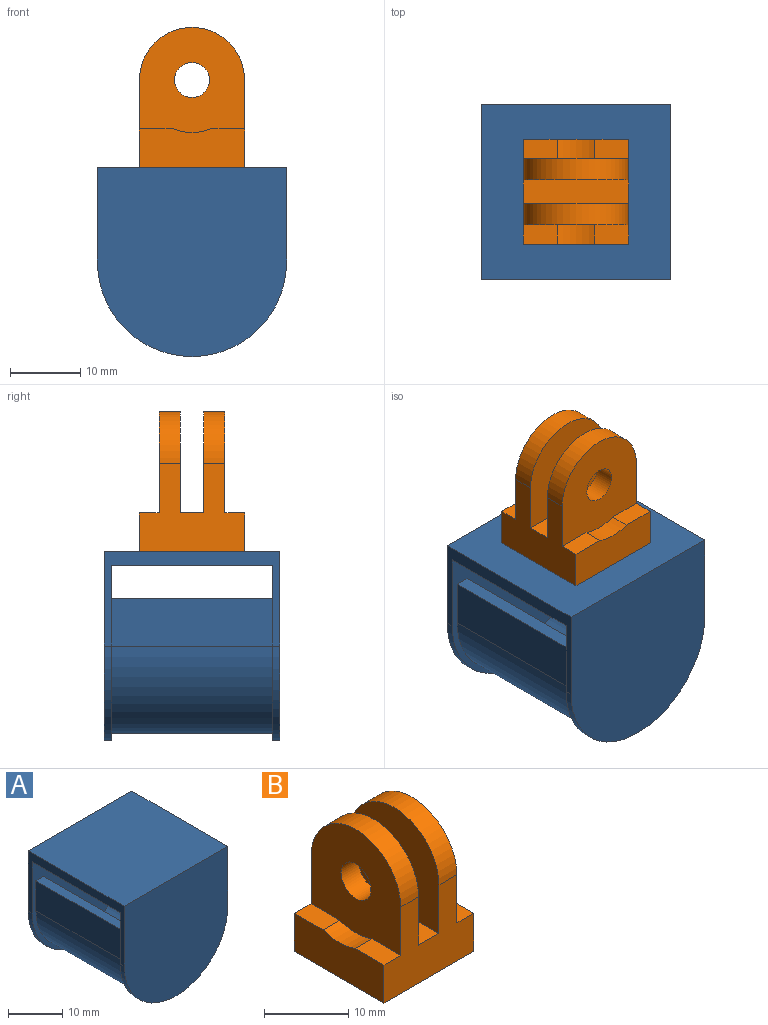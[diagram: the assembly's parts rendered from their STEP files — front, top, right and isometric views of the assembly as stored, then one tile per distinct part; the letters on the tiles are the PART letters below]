
ASSEMBLY  parts=2 mates=1
PART A: 18 faces, bbox 27x25x27 mm
  f0: plane 23x6.75mm, normal (1,0,0), area 155.2mm2, adj f3,f11,f13,f17
  f1: plane 27x23mm, normal (0,0,-1), area 621mm2, adj f4,f6,f13,f17
  f2: plane 23x6.75mm, normal (-1,0,0), area 155.2mm2, adj f3,f12,f13,f17
  f3: cylinder r=12.5mm len=25mm, axis (0,1,0), area 903.2mm2, adj f0,f2,f13,f17
  f4: plane 25x13.5mm, normal (1,0,0), area 73mm2, adj f1,f5,f7,f8,f9,f10,f13,f17
  f5: plane 27x25mm, normal (0,0,1), area 675mm2, adj f4,f6,f7,f8
  f6: plane 25x13.5mm, normal (-1,0,0), area 73mm2, adj f1,f5,f7,f8,f9,f10,f13,f17
  f7: plane 27x27mm, normal (0,-1,0), area 650.8mm2, adj f4,f5,f6,f10
  f8: plane 27x27mm, normal (0,1,0), area 650.8mm2, adj f4,f5,f6,f9
  f9: cylinder r=13.5mm len=27mm, axis (0,1,0), area 42.4mm2, adj f4,f6,f8,f13
  f10: cylinder r=13.5mm len=27mm, axis (0,1,0), area 42.4mm2, adj f4,f6,f7,f17
  f11: plane 23x2mm, normal (0,0,1), area 46mm2, adj f0,f13,f15,f17
  f12: plane 23x2mm, normal (0,0,1), area 46mm2, adj f2,f13,f14,f17
  f13: plane 27x25mm, normal (0,-1,0), area 497.5mm2, adj f0,f1,f2,f3,f4,f6,f9,f11
  f14: plane 23x6.75mm, normal (1,0,0), area 155.2mm2, adj f12,f13,f16,f17
  f15: plane 23x6.75mm, normal (-1,0,0), area 155.2mm2, adj f11,f13,f16,f17
  f16: cylinder r=10.5mm len=23mm, axis (0,1,0), area 758.7mm2, adj f13,f14,f15,f17
  f17: plane 27x25mm, normal (0,1,0), area 497.5mm2, adj f0,f1,f2,f3,f4,f6,f10,f11
PART B: 20 faces, bbox 15x15x20 mm
  f0: plane 4.81x2.8mm, normal (0,0,1), area 13.5mm2, adj f3,f8,f11,f19
  f1: plane 15x5.5mm, normal (-1,0,0), area 80.7mm2, adj f2,f3,f6,f7,f9,f18
  f2: plane 4.81x2.8mm, normal (0,0,1), area 13.5mm2, adj f1,f6,f10,f18
  f3: plane 15x12.5mm, normal (0,1,0), area 124.5mm2, adj f0,f1,f4,f5,f7,f8,f9,f10
  f4: cylinder r=7.5mm len=15mm, axis (-1,0,0), area 70.7mm2, adj f3,f6,f11,f14
  f5: cylinder r=7.5mm len=15mm, axis (-1,0,0), area 70.7mm2, adj f3,f6,f10,f15
  f6: plane 15x12.5mm, normal (0,-1,0), area 124.5mm2, adj f1,f2,f4,f5,f7,f8,f10,f11
  f7: plane 15x15mm, normal (0,0,-1), area 225mm2, adj f1,f3,f6,f8
  f8: plane 15x5.5mm, normal (1,0,0), area 80.7mm2, adj f0,f3,f6,f7,f12,f19
  f9: plane 4.81x2.8mm, normal (0,0,1), area 13.5mm2, adj f1,f3,f10,f18
  f10: plane 15x15mm, normal (-1,0,0), area 175.5mm2, adj f2,f3,f5,f6,f9,f16,f18
  f11: plane 15x15mm, normal (1,0,0), area 175.5mm2, adj f0,f3,f4,f6,f12,f17,f19
  f12: plane 4.81x2.8mm, normal (0,0,1), area 13.5mm2, adj f6,f8,f11,f19
  f13: plane 15x3.4mm, normal (0,0,1), area 51mm2, adj f3,f6,f14,f15
  f14: plane 15x14.5mm, normal (-1,0,0), area 173.7mm2, adj f3,f4,f6,f13,f17
  f15: plane 15x14.5mm, normal (1,0,0), area 173.7mm2, adj f3,f5,f6,f13,f16
  f16: cylinder r=2.5mm len=5mm, axis (-1,0,0), area 47.1mm2, adj f10,f15
  f17: cylinder r=2.5mm len=5mm, axis (-1,0,0), area 47.1mm2, adj f11,f14
  f18: cylinder r=7.5mm len=5.39mm, axis (-1,0,0), area 15.4mm2, adj f1,f2,f9,f10
  f19: cylinder r=7.5mm len=5.39mm, axis (1,0,0), area 15.4mm2, adj f0,f8,f11,f12
PLACE A at identity
PLACE B rot(axis=(0,0,1),90deg) t=(-1.93,-12.5,28.02)mm
MATE planar B.f7 <-> A.f5  axis (0,0,-1) through (-1.93,-12.5,15.52)mm
